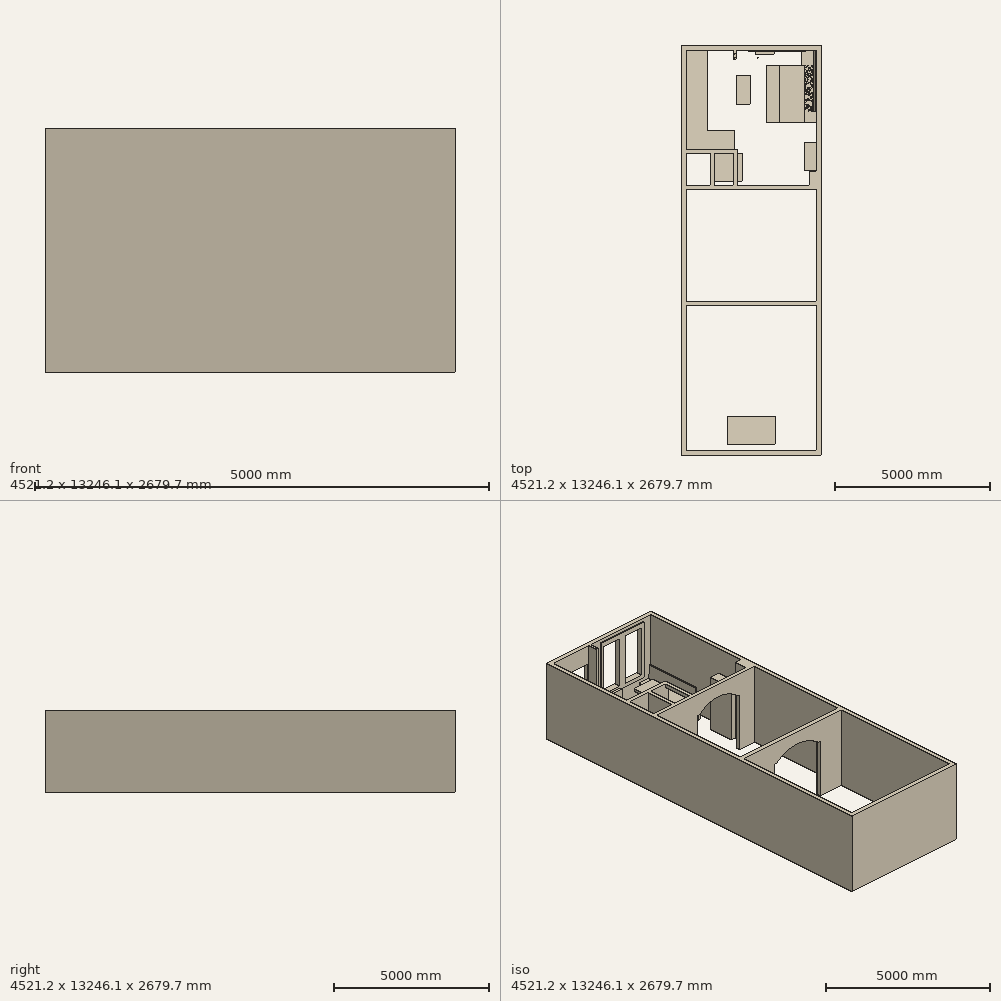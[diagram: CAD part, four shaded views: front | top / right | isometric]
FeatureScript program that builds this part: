
annotation { "Feature Type Name" : "Feature", "Feature Type Description" : "" }
export const myFeature = defineFeature(function(context is Context, id is Id, definition is map)
    precondition{}
    {
        {
            var Q0;
            Q0=qCreatedBy(makeId("Top.planeOp"),FACE);
            var sketch = newSketch(context, id + "F0", { "sketchPlane" : qUnion([Q0])});
            skLineSegment(sketch, "E0.bottom", {"start": v(0, 0) * mm, "end": v(4216.4, 0) * mm});
            skLineSegment(sketch, "E0.top", {"start": v(0, 12941.3) * mm, "end": v(1536.7, 12941.3) * mm});
            skLineSegment(sketch, "E0.left", {"start": v(0, 0) * mm, "end": v(0, 4686.3) * mm});
            skLineSegment(sketch, "E0.right", {"start": v(4216.4, 0) * mm, "end": v(4216.4, 4686.3) * mm});
            skLineSegment(sketch, "E1.bottom", {"start": v(4216.4, 4686.3) * mm, "end": v(3314.7, 4686.3) * mm});
            skLineSegment(sketch, "E1.top", {"start": v(4216.4, 4838.7) * mm, "end": v(3314.7, 4838.7) * mm});
            skLineSegment(sketch, "E1.right", {"start": v(3314.7, 4686.3) * mm, "end": v(3314.7, 4838.7) * mm});
            skLineSegment(sketch, "E2.0", {"start": v(-152.4, 13093.7) * mm, "end": v(4368.8, 13093.7) * mm});
            skLineSegment(sketch, "E2.1", {"start": v(-152.4, -152.4) * mm, "end": v(-152.4, 13093.7) * mm});
            skLineSegment(sketch, "E2.2", {"start": v(-152.4, -152.4) * mm, "end": v(4368.8, -152.4) * mm});
            skLineSegment(sketch, "E2.3", {"start": v(4368.8, -152.4) * mm, "end": v(4368.8, 13093.7) * mm});
            skLineSegment(sketch, "E3.trimOffspring", {"start": v(4216.4, 4838.7) * mm, "end": v(4216.4, 8445.5) * mm});
            skLineSegment(sketch, "E4", {"start": v(4216.4, 8445.5) * mm, "end": v(3581.4, 8445.5) * mm});
            skLineSegment(sketch, "E5", {"start": v(3581.4, 8445.5) * mm, "end": v(3581.4, 8572.5) * mm});
            skLineSegment(sketch, "E6", {"start": v(3581.4, 8572.5) * mm, "end": v(3987.8, 8572.5) * mm});
            skLineSegment(sketch, "E7.trimOffspring", {"start": v(4216.4, 9029.7) * mm, "end": v(4216.4, 12941.3) * mm});
            skLineSegment(sketch, "E8", {"start": v(3987.8, 8572.5) * mm, "end": v(3987.8, 9029.7) * mm});
            skLineSegment(sketch, "E9", {"start": v(3987.8, 9029.7) * mm, "end": v(4216.4, 9029.7) * mm});
            skLineSegment(sketch, "E10", {"start": v(1752.6, 8445.5) * mm, "end": v(0, 8445.5) * mm});
            skLineSegment(sketch, "E11", {"start": v(1752.6, 8445.5) * mm, "end": v(1752.6, 8572.5) * mm});
            skLineSegment(sketch, "E12", {"start": v(1752.6, 8572.5) * mm, "end": v(1663.7, 8572.5) * mm});
            skLineSegment(sketch, "E13", {"start": v(1663.7, 8572.5) * mm, "end": v(1663.7, 9740.9) * mm});
            skLineSegment(sketch, "E14", {"start": v(1663.7, 9740.9) * mm, "end": v(0, 9740.9) * mm});
            skLineSegment(sketch, "E15.0", {"start": v(1536.7, 9613.9) * mm, "end": v(901.7, 9613.9) * mm});
            skLineSegment(sketch, "E15.1", {"start": v(1536.7, 8572.5) * mm, "end": v(1536.7, 9613.9) * mm});
            skLineSegment(sketch, "E16", {"start": v(1536.7, 8572.5) * mm, "end": v(901.7, 8572.5) * mm});
            skLineSegment(sketch, "E17.trimOffspring", {"start": v(0, 8572.5) * mm, "end": v(0, 9613.9) * mm});
            skLineSegment(sketch, "E18.trimOffspring", {"start": v(0, 9740.9) * mm, "end": v(0, 12941.3) * mm});
            skLineSegment(sketch, "E19.top", {"start": v(1536.7, 12077.7) * mm, "end": v(1625.6, 12077.7) * mm, "construction": true});
            skLineSegment(sketch, "E19.left", {"start": v(1536.7, 12941.3) * mm, "end": v(1536.7, 12636.5) * mm});
            skLineSegment(sketch, "E19.right", {"start": v(1625.6, 12941.3) * mm, "end": v(1625.6, 12636.5) * mm});
            skLineSegment(sketch, "E20.trimOffspring", {"start": v(1625.6, 12941.3) * mm, "end": v(4216.4, 12941.3) * mm});
            skLineSegment(sketch, "E21.bottom", {"start": v(1333.5, 4838.7) * mm, "end": v(0, 4838.7) * mm});
            skLineSegment(sketch, "E21.top", {"start": v(1333.5, 4686.3) * mm, "end": v(0, 4686.3) * mm});
            skLineSegment(sketch, "E21.left", {"start": v(1333.5, 4838.7) * mm, "end": v(1333.5, 4686.3) * mm});
            skLineSegment(sketch, "E22.trimOffspring", {"start": v(0, 4838.7) * mm, "end": v(0, 8445.5) * mm});
            skLineSegment(sketch, "E23.left", {"start": v(774.7, 9613.9) * mm, "end": v(774.7, 8572.5) * mm});
            skLineSegment(sketch, "E23.right", {"start": v(901.7, 9613.9) * mm, "end": v(901.7, 8572.5) * mm});
            skLineSegment(sketch, "E24.trimOffspring", {"start": v(774.7, 9613.9) * mm, "end": v(0, 9613.9) * mm});
            skLineSegment(sketch, "E25.trimOffspring", {"start": v(774.7, 8572.5) * mm, "end": v(0, 8572.5) * mm});
            skLineSegment(sketch, "E26", {"start": v(1536.7, 12636.5) * mm, "end": v(1625.6, 12636.5) * mm});
            skSolve(sketch);
        }
        {
            var Q0;
            Q0=makeQuery(id+"F0.imprint","IMPRINT",FACE,{"disambiguationData":[TD([[makeQuery(id+"F0.imprint","IMPRINT",EDGE,{"derivedFrom":sQuery(id+"F0.wireOp",EDGE,"E0.bottom")}),-1.0]])]});
            extrude(context, id + "F1", {"entities" : qUnion([Q0]), "depth" : 2679.7 * mm});
        }
        {
            var Q0;
            Q0=makeQuery(id+"F1.opExtrude","SWEPT_FACE",FACE,{"disambiguationData":[OSD([sQuery(id+"F0.wireOp",EDGE,"E21.top")])]});
            var sketch = newSketch(context, id + "F2", { "sketchPlane" : qUnion([Q0])});
            skLineSegment(sketch, "E27.bottom", {"start": v(1333.5, 2679.7) * mm, "end": v(3314.7, 2679.7) * mm});
            skLineSegment(sketch, "E27.top", {"start": v(1333.5, 1930.4) * mm, "end": v(1422.4, 1930.4) * mm});
            skLineSegment(sketch, "E27.left", {"start": v(1333.5, 2679.7) * mm, "end": v(1333.5, 1930.4) * mm});
            skLineSegment(sketch, "E27.right", {"start": v(3314.7, 2679.7) * mm, "end": v(3314.7, 1930.4) * mm});
            skLineSegment(sketch, "E28", {"start": v(2324.1, 1930.4) * mm, "end": v(2324.1, 2679.7) * mm, "construction": true});
            skLineSegment(sketch, "E29", {"start": v(1422.4, 1930.4) * mm, "end": v(1422.4, 2679.7) * mm, "construction": true});
            skLineSegment(sketch, "E30", {"start": v(3225.8, 1930.4) * mm, "end": v(3225.8, 2679.7) * mm, "construction": true});
            skLineSegment(sketch, "E31", {"start": v(1422.4, 2247.9) * mm, "end": v(3225.8, 2247.9) * mm, "construction": true});
            skArc(sketch, "E32", {"start": v(3225.8, 1930.4) * mm, "mid": v(2324.1, 2247.9) * mm, "end": v(1422.4, 1930.4) * mm});
            skLineSegment(sketch, "E33.trimOffspring", {"start": v(3225.8, 1930.4) * mm, "end": v(3314.7, 1930.4) * mm});
            skSolve(sketch);
        }
        {
            var Q0;
            Q0=makeQuery(id+"F2.imprint","IMPRINT",FACE,{"disambiguationData":[TD([[makeQuery(id+"F2.imprint","IMPRINT",EDGE,{"derivedFrom":sQuery(id+"F2.wireOp",EDGE,"E27.bottom")}),-1.0]])]});
            extrude(context, id + "F3", {"entities" : qUnion([Q0]), "operationType" : NewBodyOperationType.ADD, "oppositeDirection" : true, "depth" : 152.4 * mm});
        }
        {
            var Q0;
            Q0=makeQuery(id+"F1.opExtrude","SWEPT_FACE",FACE,{"disambiguationData":[OSD([sQuery(id+"F0.wireOp",EDGE,"E10")])]});
            var sketch = newSketch(context, id + "F4", { "sketchPlane" : qUnion([Q0])});
            skLineSegment(sketch, "E34.bottom", {"start": v(1752.6, 2679.7) * mm, "end": v(3581.4, 2679.7) * mm});
            skLineSegment(sketch, "E34.top", {"start": v(1752.6, 1930.4) * mm, "end": v(1841.5, 1930.4) * mm});
            skLineSegment(sketch, "E34.left", {"start": v(1752.6, 2679.7) * mm, "end": v(1752.6, 1930.4) * mm});
            skLineSegment(sketch, "E34.right", {"start": v(3581.4, 2679.7) * mm, "end": v(3581.4, 1930.4) * mm});
            skLineSegment(sketch, "E35", {"start": v(2667, 1930.4) * mm, "end": v(2667, 2679.7) * mm, "construction": true});
            skLineSegment(sketch, "E36", {"start": v(1841.5, 1930.4) * mm, "end": v(1841.5, 2679.7) * mm, "construction": true});
            skLineSegment(sketch, "E37", {"start": v(3492.5, 1930.4) * mm, "end": v(3492.5, 2679.7) * mm, "construction": true});
            skLineSegment(sketch, "E38", {"start": v(1841.5, 2247.9) * mm, "end": v(3492.5, 2247.9) * mm, "construction": true});
            skArc(sketch, "E39", {"start": v(3492.5, 1930.4) * mm, "mid": v(2667, 2247.9) * mm, "end": v(1841.5, 1930.4) * mm});
            skLineSegment(sketch, "E40.trimOffspring", {"start": v(3492.5, 1930.4) * mm, "end": v(3581.4, 1930.4) * mm});
            skSolve(sketch);
        }
        {
            var Q0;
            Q0=qSketchRegion(id+"F4",true);
            extrude(context, id + "F5", {"entities" : qUnion([Q0]), "operationType" : NewBodyOperationType.ADD, "oppositeDirection" : true, "depth" : 127 * mm});
        }
        {
            var Q0;
            Q0=makeQuery(id+"F1.opExtrude","CAP_FACE",FACE,{"disambiguationData":[OSD([sQuery(id+"F0.wireOp",EDGE,"E0.bottom"),sQuery(id+"F0.wireOp",EDGE,"E0.top"),sQuery(id+"F0.wireOp",EDGE,"E0.left"),sQuery(id+"F0.wireOp",EDGE,"E0.right"),sQuery(id+"F0.wireOp",EDGE,"E1.bottom"),sQuery(id+"F0.wireOp",EDGE,"E1.top"),sQuery(id+"F0.wireOp",EDGE,"E1.right"),sQuery(id+"F0.wireOp",EDGE,"E2.0"),sQuery(id+"F0.wireOp",EDGE,"E2.1"),sQuery(id+"F0.wireOp",EDGE,"E2.2"),sQuery(id+"F0.wireOp",EDGE,"E2.3"),sQuery(id+"F0.wireOp",EDGE,"E3.trimOffspring"),sQuery(id+"F0.wireOp",EDGE,"E4"),sQuery(id+"F0.wireOp",EDGE,"E5"),sQuery(id+"F0.wireOp",EDGE,"E6"),sQuery(id+"F0.wireOp",EDGE,"E7.trimOffspring"),sQuery(id+"F0.wireOp",EDGE,"E8"),sQuery(id+"F0.wireOp",EDGE,"E9"),sQuery(id+"F0.wireOp",EDGE,"E10"),sQuery(id+"F0.wireOp",EDGE,"E11"),sQuery(id+"F0.wireOp",EDGE,"E12"),sQuery(id+"F0.wireOp",EDGE,"E13"),sQuery(id+"F0.wireOp",EDGE,"E14"),sQuery(id+"F0.wireOp",EDGE,"E15.0"),sQuery(id+"F0.wireOp",EDGE,"E15.1"),sQuery(id+"F0.wireOp",EDGE,"E16"),sQuery(id+"F0.wireOp",EDGE,"E17.trimOffspring"),sQuery(id+"F0.wireOp",EDGE,"E18.trimOffspring"),sQuery(id+"F0.wireOp",EDGE,"E19.top"),sQuery(id+"F0.wireOp",EDGE,"E19.left"),sQuery(id+"F0.wireOp",EDGE,"E19.right"),sQuery(id+"F0.wireOp",EDGE,"E20.trimOffspring"),sQuery(id+"F0.wireOp",EDGE,"E21.bottom"),sQuery(id+"F0.wireOp",EDGE,"E21.top"),sQuery(id+"F0.wireOp",EDGE,"E21.left"),sQuery(id+"F0.wireOp",EDGE,"E22.trimOffspring")])],"isStart":true});
            var sketch = newSketch(context, id + "F6", { "sketchPlane" : qUnion([Q0])});
            skLineSegment(sketch, "E41.bottom", {"start": v(0, -12941.3) * mm, "end": v(673.1, -12941.3) * mm});
            skLineSegment(sketch, "E41.top", {"start": v(0, -9740.9) * mm, "end": v(1562.1, -9740.9) * mm});
            skLineSegment(sketch, "E41.left", {"start": v(0, -12941.3) * mm, "end": v(0, -9740.9) * mm});
            skLineSegment(sketch, "E42.top", {"start": v(1562.1, -10337.8) * mm, "end": v(673.1, -10337.8) * mm});
            skLineSegment(sketch, "E42.left", {"start": v(1562.1, -9740.9) * mm, "end": v(1562.1, -10337.8) * mm});
            skLineSegment(sketch, "E43", {"start": v(673.1, -10337.8) * mm, "end": v(673.1, -12941.3) * mm});
            skSolve(sketch);
        }
        {
            var Q0;
            Q0=qSketchRegion(id+"F6",true);
            extrude(context, id + "F7", {"entities" : qUnion([Q0]), "operationType" : NewBodyOperationType.ADD, "oppositeDirection" : true, "depth" : 914.4 * mm});
        }
        {
            var Q0;
            Q0=makeQuery(id+"F1.opExtrude","SWEPT_FACE",FACE,{"disambiguationData":[OSD([sQuery(id+"F0.wireOp",EDGE,"E0.top"),sQuery(id+"F0.wireOp",EDGE,"E20.trimOffspring"),sQuery(id+"F0.wireOp",EDGE,"cWmxFn2V-QyjY-M4hI-rjAM-pF5ntR53oyUy")])]});
            var sketch = newSketch(context, id + "F8", { "sketchPlane" : qUnion([Q0])});
            skLineSegment(sketch, "E44.bottom", {"start": v(3886.2, 2565.4) * mm, "end": v(2019.3, 2565.4) * mm});
            skLineSegment(sketch, "E44.top", {"start": v(3886.2, 609.6) * mm, "end": v(2019.3, 609.6) * mm});
            skLineSegment(sketch, "E44.left", {"start": v(3886.2, 2565.4) * mm, "end": v(3886.2, 609.6) * mm});
            skLineSegment(sketch, "E44.right", {"start": v(2019.3, 2565.4) * mm, "end": v(2019.3, 609.6) * mm});
            skSolve(sketch);
        }
        {
            var Q0;
            Q0 = qSketchRegion(id + "F8", true);
            extrude(context, id + "F9", {"entities" : qUnion([Q0]), "operationType" : NewBodyOperationType.ADD, "depth" : 50.8 * mm});
        }
        {
            var Q0;
            Q0=makeQuery(id+"F1.opExtrude","SWEPT_FACE",FACE,{"disambiguationData":[OSD([sQuery(id+"F0.wireOp",EDGE,"E20.trimOffspring")])]});
            var sketch = newSketch(context, id + "F10", { "sketchPlane" : qUnion([Q0])});
            skLineSegment(sketch, "E45.bottom", {"start": v(2133.6, 2413) * mm, "end": v(2819.4, 2413) * mm});
            skLineSegment(sketch, "E45.top", {"start": v(2133.6, 736.6) * mm, "end": v(2819.4, 736.6) * mm});
            skLineSegment(sketch, "E45.left", {"start": v(2133.6, 2413) * mm, "end": v(2133.6, 736.6) * mm});
            skLineSegment(sketch, "E45.right", {"start": v(2819.4, 2413) * mm, "end": v(2819.4, 736.6) * mm});
            skLineSegment(sketch, "E46.bottom", {"start": v(3086.1, 2413) * mm, "end": v(3771.9, 2413) * mm});
            skLineSegment(sketch, "E46.top", {"start": v(3086.1, 736.6) * mm, "end": v(3771.9, 736.6) * mm});
            skLineSegment(sketch, "E46.left", {"start": v(3086.1, 2413) * mm, "end": v(3086.1, 736.6) * mm});
            skLineSegment(sketch, "E46.right", {"start": v(3771.9, 2413) * mm, "end": v(3771.9, 736.6) * mm});
            skSolve(sketch);
        }
        {
            var Q0;
            Q0=qSketchRegion(id+"F10",true);
            extrude(context, id + "F11", {"entities" : qUnion([Q0]), "operationType" : NewBodyOperationType.REMOVE, "endBound" : BoundingType.UP_TO_NEXT, "oppositeDirection" : true, "depth" : 25.4 * mm, "hasSecondDirection" : true, "secondDirectionBound" : BoundingType.UP_TO_NEXT, "secondDirectionOppositeDirection" : false, "secondDirectionDepth" : 25.4 * mm});
        }
        {
            var Q0;
            Q0=makeQuery(id+"F1.opExtrude","SWEPT_FACE",FACE,{"disambiguationData":[OSD([sQuery(id+"F0.wireOp",EDGE,"E0.top"),sQuery(id+"F0.wireOp",EDGE,"E20.trimOffspring"),sQuery(id+"F0.wireOp",EDGE,"cWmxFn2V-QyjY-M4hI-rjAM-pF5ntR53oyUy")])]});
            var sketch = newSketch(context, id + "F12", { "sketchPlane" : qUnion([Q0])});
            skLineSegment(sketch, "E47.bottom", {"start": v(723.9, 0) * mm, "end": v(1485.9, 0) * mm});
            skLineSegment(sketch, "E47.top", {"start": v(723.9, 2032) * mm, "end": v(1485.9, 2032) * mm});
            skLineSegment(sketch, "E47.left", {"start": v(723.9, 0) * mm, "end": v(723.9, 2032) * mm});
            skLineSegment(sketch, "E47.right", {"start": v(1485.9, 0) * mm, "end": v(1485.9, 2032) * mm});
            skSolve(sketch);
        }
        {
            var Q0;
            Q0 = qSketchRegion(id + "F12", true);
            extrude(context, id + "F13", {"entities" : qUnion([Q0]), "operationType" : NewBodyOperationType.REMOVE, "endBound" : BoundingType.UP_TO_NEXT, "oppositeDirection" : true, "depth" : 25.4 * mm});
        }
        {
            var Q0;
            Q0=makeQuery(id+"F1.opExtrude","SWEPT_FACE",FACE,{"disambiguationData":[OSD([sQuery(id+"F0.wireOp",EDGE,"E20.trimOffspring")])]});
            var sketch = newSketch(context, id + "F14", { "sketchPlane" : qUnion([Q0])});
            skLineSegment(sketch, "E48.bottom", {"start": v(2997.2, 762) * mm, "end": v(3810, 762) * mm});
            skLineSegment(sketch, "E48.top", {"start": v(3302, 0) * mm, "end": v(3505.2, 0) * mm});
            skLineSegment(sketch, "E48.left", {"start": v(2997.2, 762) * mm, "end": v(2997.2, 660.4) * mm});
            skLineSegment(sketch, "E48.right", {"start": v(3810, 762) * mm, "end": v(3810, 660.4) * mm});
            skLineSegment(sketch, "E49", {"start": v(2997.2, 660.4) * mm, "end": v(3302, 660.4) * mm});
            skLineSegment(sketch, "E50", {"start": v(3302, 660.4) * mm, "end": v(3302, 0) * mm});
            skLineSegment(sketch, "E51", {"start": v(3810, 660.4) * mm, "end": v(3505.2, 660.4) * mm});
            skLineSegment(sketch, "E52", {"start": v(3505.2, 660.4) * mm, "end": v(3505.2, 0) * mm});
            skLineSegment(sketch, "E53", {"start": v(2768.6, 0) * mm, "end": v(2768.6, 355.6) * mm});
            skLineSegment(sketch, "E54", {"start": v(2768.6, 355.6) * mm, "end": v(2590.8, 355.6) * mm});
            skLineSegment(sketch, "E55", {"start": v(2590.8, 355.6) * mm, "end": v(2590.8, 457.2) * mm});
            skLineSegment(sketch, "E56", {"start": v(2590.8, 457.2) * mm, "end": v(3048, 457.2) * mm});
            skLineSegment(sketch, "E57", {"start": v(3048, 457.2) * mm, "end": v(3048, 355.6) * mm});
            skLineSegment(sketch, "E58", {"start": v(3048, 355.6) * mm, "end": v(2870.2, 355.6) * mm});
            skLineSegment(sketch, "E59", {"start": v(2870.2, 355.6) * mm, "end": v(2870.2, 0) * mm});
            skLineSegment(sketch, "E60", {"start": v(2870.2, 0) * mm, "end": v(2768.6, 0) * mm});
            skLineSegment(sketch, "E61", {"start": v(2819.4, 0) * mm, "end": v(2819.4, 457.2) * mm, "construction": true});
            skLineSegment(sketch, "E62", {"start": v(3403.6, 0) * mm, "end": v(3403.6, 762) * mm, "construction": true});
            skLineSegment(sketch, "E63.MirrorCS", {"start": v(3759.2, 457.2) * mm, "end": v(3759.2, 355.6) * mm});
            skLineSegment(sketch, "E64.MirrorCS", {"start": v(4216.4, 457.2) * mm, "end": v(3759.2, 457.2) * mm});
            skLineSegment(sketch, "E65.MirrorCS", {"start": v(4216.4, 355.6) * mm, "end": v(4216.4, 457.2) * mm});
            skLineSegment(sketch, "E66.MirrorCS", {"start": v(4038.6, 355.6) * mm, "end": v(4216.4, 355.6) * mm});
            skLineSegment(sketch, "E67.MirrorCS", {"start": v(4038.6, 0) * mm, "end": v(4038.6, 355.6) * mm});
            skLineSegment(sketch, "E68.MirrorCS", {"start": v(3937, 355.6) * mm, "end": v(3937, 0) * mm});
            skLineSegment(sketch, "E69.MirrorCS", {"start": v(3759.2, 355.6) * mm, "end": v(3937, 355.6) * mm});
            skLineSegment(sketch, "E70.MirrorCS", {"start": v(3937, 0) * mm, "end": v(4038.6, 0) * mm});
            skSolve(sketch);
        }
        {
            var Q0;
            Q0=qSketchRegion(id+"F14",true);
            extrude(context, id + "F15", {"entities" : qUnion([Q0]), "depth" : 2336.8 * mm, "hasSecondDirection" : true, "secondDirectionOppositeDirection" : false, "secondDirectionDepth" : 508 * mm, "offsetDistance" : 25.4 * mm});
        }
        {
            var Q0;
            Q0=qCreatedBy(makeId("Top.planeOp"),FACE);
            var sketch = newSketch(context, id + "F16", { "sketchPlane" : qUnion([Q0])});
            skLineSegment(sketch, "E71.bottom", {"start": v(4203.7, 9956.8) * mm, "end": v(3822.7, 9956.8) * mm});
            skLineSegment(sketch, "E71.top", {"start": v(3822.7, 9042.4) * mm, "end": v(4203.7, 9042.4) * mm});
            skLineSegment(sketch, "E71.left", {"start": v(4203.7, 9956.8) * mm, "end": v(4203.7, 9042.4) * mm});
            skLineSegment(sketch, "E71.right", {"start": v(3822.7, 9956.8) * mm, "end": v(3822.7, 9042.4) * mm});
            skSolve(sketch);
        }
        {
            var Q0;
            Q0=qSketchRegion(id+"F16",true);
            extrude(context, id + "F17", {"entities" : qUnion([Q0]), "operationType" : NewBodyOperationType.ADD, "depth" : 1828.8 * mm});
        }
        {
            var Q0;
            Q0=makeQuery(id+"F1.opExtrude","SWEPT_FACE",FACE,{"disambiguationData":[OSD([sQuery(id+"F0.wireOp",EDGE,"E13")])]});
            var sketch = newSketch(context, id + "F18", { "sketchPlane" : qUnion([Q0])});
            skLineSegment(sketch, "E72.bottom", {"start": v(8674.1, 0) * mm, "end": v(9613.9, 0) * mm});
            skLineSegment(sketch, "E72.top", {"start": v(8674.1, 1879.6) * mm, "end": v(9613.9, 1879.6) * mm});
            skLineSegment(sketch, "E72.left", {"start": v(8674.1, 0) * mm, "end": v(8674.1, 1879.6) * mm});
            skLineSegment(sketch, "E72.right", {"start": v(9613.9, 0) * mm, "end": v(9613.9, 1879.6) * mm});
            skLineSegment(sketch, "E73.bottom", {"start": v(8674.1, 2006.6) * mm, "end": v(9613.9, 2006.6) * mm});
            skLineSegment(sketch, "E73.top", {"start": v(8674.1, 2552.7) * mm, "end": v(9613.9, 2552.7) * mm});
            skLineSegment(sketch, "E73.left", {"start": v(8674.1, 2006.6) * mm, "end": v(8674.1, 2552.7) * mm});
            skLineSegment(sketch, "E73.right", {"start": v(9613.9, 2006.6) * mm, "end": v(9613.9, 2552.7) * mm});
            skSolve(sketch);
        }
        {
            var Q0;
            Q0 = qSketchRegion(id + "F18", true);
            var Q1;
            Q1=makeQuery(id+"F1.opExtrude","SWEPT_FACE",FACE,{"disambiguationData":[OSD([sQuery(id+"F0.wireOp",EDGE,"E15.1")])]});
            extrude(context, id + "F19", {"entities" : qUnion([Q0]), "operationType" : NewBodyOperationType.REMOVE, "endBound" : BoundingType.UP_TO_SURFACE, "oppositeDirection" : true, "endBoundEntityFace" : qUnion([Q1]), "depth" : 25.4 * mm});
        }
        {
            var Q0;
            Q0=qCreatedBy(makeId("Top.planeOp"),FACE);
            var sketch = newSketch(context, id + "F20", { "sketchPlane" : qUnion([Q0])});
            skLineSegment(sketch, "E74.bottom", {"start": v(927.1, 9601.2) * mm, "end": v(1816.1, 9601.2) * mm});
            skLineSegment(sketch, "E74.top", {"start": v(927.1, 8686.8) * mm, "end": v(1816.1, 8686.8) * mm});
            skLineSegment(sketch, "E74.left", {"start": v(927.1, 9601.2) * mm, "end": v(927.1, 8686.8) * mm});
            skLineSegment(sketch, "E74.right", {"start": v(1816.1, 9601.2) * mm, "end": v(1816.1, 8686.8) * mm});
            skSolve(sketch);
        }
        {
            var Q0;
            Q0=makeQuery(id+"F20.imprint","IMPRINT",FACE,{"disambiguationData":[TD([[makeQuery(id+"F20.imprint","IMPRINT",EDGE,{"derivedFrom":sQuery(id+"F20.wireOp",EDGE,"E74.bottom")}),-1.0]])]});
            extrude(context, id + "F21", {"entities" : qUnion([Q0]), "operationType" : NewBodyOperationType.ADD, "depth" : 1778 * mm});
        }
        {
            var Q0;
            Q0=qCreatedBy(makeId("Top.planeOp"),FACE);
            var sketch = newSketch(context, id + "F22", { "sketchPlane" : qUnion([Q0])});
            skLineSegment(sketch, "E75.bottom", {"start": v(1638.3, 12115.8) * mm, "end": v(2082.8, 12115.8) * mm});
            skLineSegment(sketch, "E75.top", {"start": v(1638.3, 11201.4) * mm, "end": v(2082.8, 11201.4) * mm});
            skLineSegment(sketch, "E75.left", {"start": v(1638.3, 12115.8) * mm, "end": v(1638.3, 11201.4) * mm});
            skLineSegment(sketch, "E75.right", {"start": v(2082.8, 12115.8) * mm, "end": v(2082.8, 11201.4) * mm});
            skSolve(sketch);
        }
        {
            var Q0;
            Q0=qSketchRegion(id+"F22",true);
            extrude(context, id + "F23", {"entities" : qUnion([Q0]), "depth" : 914.4 * mm, "offsetDistance" : 25.4 * mm});
        }
        {
            var Q0;
            Q0=makeQuery(id+"F5.boolean.opBoolean","MERGE",FACE,{"derivedFrom":[makeQuery(id+"F1.opExtrude","SWEPT_FACE",FACE,{"disambiguationData":[OSD([sQuery(id+"F0.wireOp",EDGE,"E4")])]}),makeQuery(id+"F1.opExtrude","SWEPT_FACE",FACE,{"disambiguationData":[OSD([sQuery(id+"F0.wireOp",EDGE,"E10")])]}),makeQuery(id+"F5.opExtrude","CAP_FACE",FACE,{"disambiguationData":[OSD([sQuery(id+"F4.wireOp",EDGE,"E34.bottom"),sQuery(id+"F4.wireOp",EDGE,"E34.top"),sQuery(id+"F4.wireOp",EDGE,"E34.left"),sQuery(id+"F4.wireOp",EDGE,"E34.right"),sQuery(id+"F4.wireOp",EDGE,"E39"),sQuery(id+"F4.wireOp",EDGE,"E40.trimOffspring")])],"isStart":true})]});
            var sketch = newSketch(context, id + "F24", { "sketchPlane" : qUnion([Q0])});
            skLineSegment(sketch, "E76.bottom", {"start": v(127, 0) * mm, "end": v(736.6, 0) * mm});
            skLineSegment(sketch, "E76.top", {"start": v(127, 2032) * mm, "end": v(736.6, 2032) * mm});
            skLineSegment(sketch, "E76.left", {"start": v(127, 0) * mm, "end": v(127, 2032) * mm});
            skLineSegment(sketch, "E76.right", {"start": v(736.6, 0) * mm, "end": v(736.6, 2032) * mm});
            skSolve(sketch);
        }
        {
            var Q0;
            Q0 = qSketchRegion(id + "F24", true);
            extrude(context, id + "F25", {"entities" : qUnion([Q0]), "operationType" : NewBodyOperationType.REMOVE, "endBound" : BoundingType.UP_TO_NEXT, "oppositeDirection" : true, "depth" : 25.4 * mm});
        }
        {
            var Q0;
            Q0=makeQuery(id+"F1.opExtrude","SWEPT_FACE",FACE,{"disambiguationData":[OSD([sQuery(id+"F0.wireOp",EDGE,"E0.top")])]});
            cPlane(context, id + "F26", {"entities" : qUnion([Q0]), "cplaneType" : CPlaneType.OFFSET, "offset" : 1981.2 * mm, "width" : 152.4 * mm, "height" : 152.4 * mm});
        }
        {
            var Q0;
            Q0=qCreatedBy(makeId("Top.planeOp"),FACE);
            var sketch = newSketch(context, id + "F27", { "sketchPlane" : qUnion([Q0])});
            skLineSegment(sketch, "E77", {"start": v(3124.2, 12941.3) * mm, "end": v(4216.4, 12941.3) * mm, "construction": true});
            skLineSegment(sketch, "E78", {"start": v(4216.4, 12941.3) * mm, "end": v(4216.4, 10960.1) * mm});
            skSolve(sketch);
        }
        {
            var Q0;
            Q0=qCreatedBy(id+"F26.planeOp",FACE);
            var sketch = newSketch(context, id + "F28", { "sketchPlane" : qUnion([Q0])});
            skLineSegment(sketch, "E79", {"start": v(4216.4, 914.4) * mm, "end": v(4165.6, 914.4) * mm});
            skLineSegment(sketch, "E80", {"start": v(4165.6, 914.4) * mm, "end": v(4125.6, 457.2) * mm});
            skLineSegment(sketch, "E81", {"start": v(4125.6, 457.2) * mm, "end": v(3719.2, 457.2) * mm});
            skLineSegment(sketch, "E82", {"start": v(3719.2, 457.2) * mm, "end": v(3719.2, 355.6) * mm});
            skLineSegment(sketch, "E83", {"start": v(3719.2, 355.6) * mm, "end": v(3911.6, 0) * mm});
            skLineSegment(sketch, "E84", {"start": v(3911.6, 0) * mm, "end": v(4216.4, 0) * mm});
            skLineSegment(sketch, "E85", {"start": v(4216.4, 0) * mm, "end": v(4216.4, 914.4) * mm});
            skSolve(sketch);
        }
        {
            var Q0;
            Q0 = qSketchRegion(id + "F28", true);
            var Q1;
            Q1 = qConstructionFilter(qBodyType(qCreatedBy(id + "F27" ,EDGE), BodyType.WIRE), ConstructionObject.NO);
            sweep(context, id + "F29", {"profiles" : qUnion([Q0]), "path" : qUnion([Q1])});
        }
        {
            var Q0;
            Q0=qCreatedBy(makeId("Top.planeOp"),FACE);
            var sketch = newSketch(context, id + "F30", { "sketchPlane" : qUnion([Q0])});
            skLineSegment(sketch, "E86", {"start": v(1574.8, 12814.3) * mm, "end": v(1574.8, 12687.3) * mm, "construction": true});
            skCircle(sketch, "E87", {"center": v(1574.8, 12814.3) * mm, "radius": 12.7 * mm});
            skCircle(sketch, "E88", {"center": v(1574.8, 12687.3) * mm, "radius": 12.7 * mm});
            skSolve(sketch);
        }
        {
            var Q0;
            Q0 = qSketchRegion(id + "F30", true);
            extrude(context, id + "F31", {"entities" : qUnion([Q0]), "depth" : 2679.7 * mm});
        }
        {
            var Q0;
            Q0=qCreatedBy(makeId("Top.planeOp"),FACE);
            var sketch = newSketch(context, id + "F32", { "sketchPlane" : qUnion([Q0]), "disableImprinting" : false});
            skLineSegment(sketch, "E89", {"start": v(2311.4, 12814.3) * mm, "end": v(2311.4, 12687.3) * mm, "construction": true});
            skCircle(sketch, "E90", {"center": v(2311.4, 12814.3) * mm, "radius": 12.7 * mm});
            skCircle(sketch, "E91", {"center": v(2311.4, 12687.3) * mm, "radius": 12.7 * mm});
            skSolve(sketch);
        }
        {
            var Q0;
            Q0 = qSketchRegion(id + "F32", true);
            extrude(context, id + "F33", {"entities" : qUnion([Q0]), "depth" : 508 * mm});
        }
        {
            var Q0;
            Q0=makeQuery(id+"F1.opExtrude","SWEPT_FACE",FACE,{"disambiguationData":[OSD([sQuery(id+"F0.wireOp",EDGE,"E20.trimOffspring")])]});
            var sketch = newSketch(context, id + "F34", { "sketchPlane" : qUnion([Q0])});
            skLineSegment(sketch, "E92.bottom", {"start": v(2247.6, 152.4) * mm, "end": v(2857.2, 152.4) * mm});
            skLineSegment(sketch, "E92.top", {"start": v(2247.6, 660.4) * mm, "end": v(2857.2, 660.4) * mm});
            skLineSegment(sketch, "E92.left", {"start": v(2247.6, 152.4) * mm, "end": v(2247.6, 660.4) * mm});
            skLineSegment(sketch, "E92.right", {"start": v(2857.2, 152.4) * mm, "end": v(2857.2, 660.4) * mm});
            skSolve(sketch);
        }
        {
            var Q0;
            Q0 = qSketchRegion(id + "F34", true);
            extrude(context, id + "F35", {"entities" : qUnion([Q0]), "depth" : 127 * mm});
        }
        {
            var Q0;
            Q0=qCreatedBy(makeId("Top.planeOp"),FACE);
            var sketch = newSketch(context, id + "F36", { "sketchPlane" : qUnion([Q0])});
            skLineSegment(sketch, "E93.bottom", {"start": v(1348.98, 1092.2) * mm, "end": v(2872.98, 1092.2) * mm});
            skLineSegment(sketch, "E93.top", {"start": v(1348.98, 203.2) * mm, "end": v(2872.98, 203.2) * mm});
            skLineSegment(sketch, "E93.left", {"start": v(1348.98, 1092.2) * mm, "end": v(1348.98, 203.2) * mm});
            skLineSegment(sketch, "E93.right", {"start": v(2872.98, 1092.2) * mm, "end": v(2872.98, 203.2) * mm});
            skSolve(sketch);
        }
        {
            var Q0;
            Q0 = qSketchRegion(id + "F36", true);
            extrude(context, id + "F37", {"entities" : qUnion([Q0]), "depth" : 838.2 * mm, "offsetDistance" : 25.4 * mm});
        }
    });
